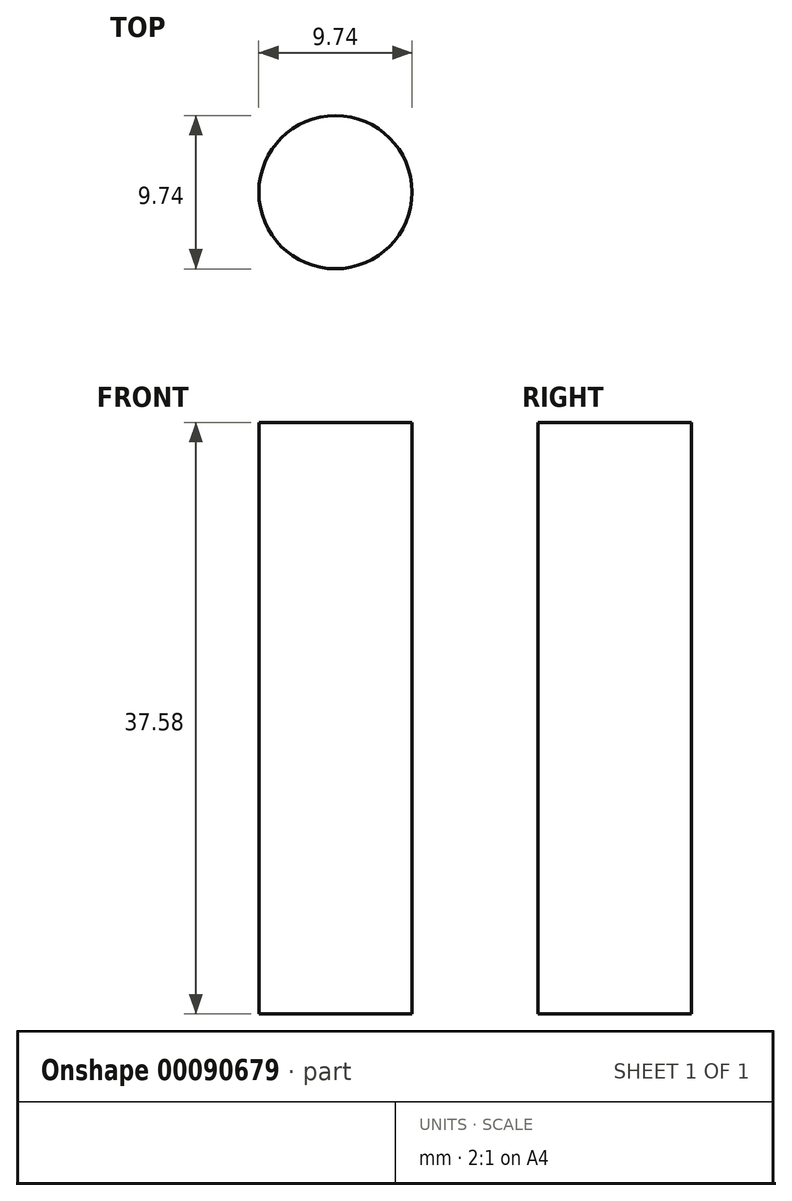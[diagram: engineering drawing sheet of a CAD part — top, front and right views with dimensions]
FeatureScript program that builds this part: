
annotation { "Feature Type Name" : "Feature", "Feature Type Description" : "" }
export const myFeature = defineFeature(function(context is Context, id is Id, definition is map)
    precondition{}
    {
        {
            var Q0;
            Q0=qCreatedBy(makeId("Front.planeOp"),FACE);
            var sketch = newSketch(context, id + "F0", { "sketchPlane" : qUnion([Q0])});
            skLineSegment(sketch, "E0", {"start": v(0, -23.79) * mm, "end": v(-4.87, -23.79) * mm});
            skLineSegment(sketch, "E1", {"start": v(-4.87, -23.79) * mm, "end": v(-4.87, 13.79) * mm});
            skLineSegment(sketch, "E2", {"start": v(-4.87, 13.79) * mm, "end": v(0, 13.79) * mm});
            skLineSegment(sketch, "E3", {"start": v(0, -23.79) * mm, "end": v(0, 13.79) * mm});
            skSolve(sketch);
        }
        {
            var Q0;
            Q0=makeQuery(id+"F0.imprint","IMPRINT",FACE,{"disambiguationData":[TD([[makeQuery(id+"F0.imprint","IMPRINT",EDGE,{"derivedFrom":sQuery(id+"F0.wireOp",EDGE,"E0")}),-1.0]])]});
            var Q1;
            Q1=sQuery(id+"F0.wireOp",EDGE,"E3");
            revolve(context, id + "F1", {"entities" : qUnion([Q0]), "axis" : qUnion([Q1]), "revolveType" : RevolveType.FULL});
        }
    });
